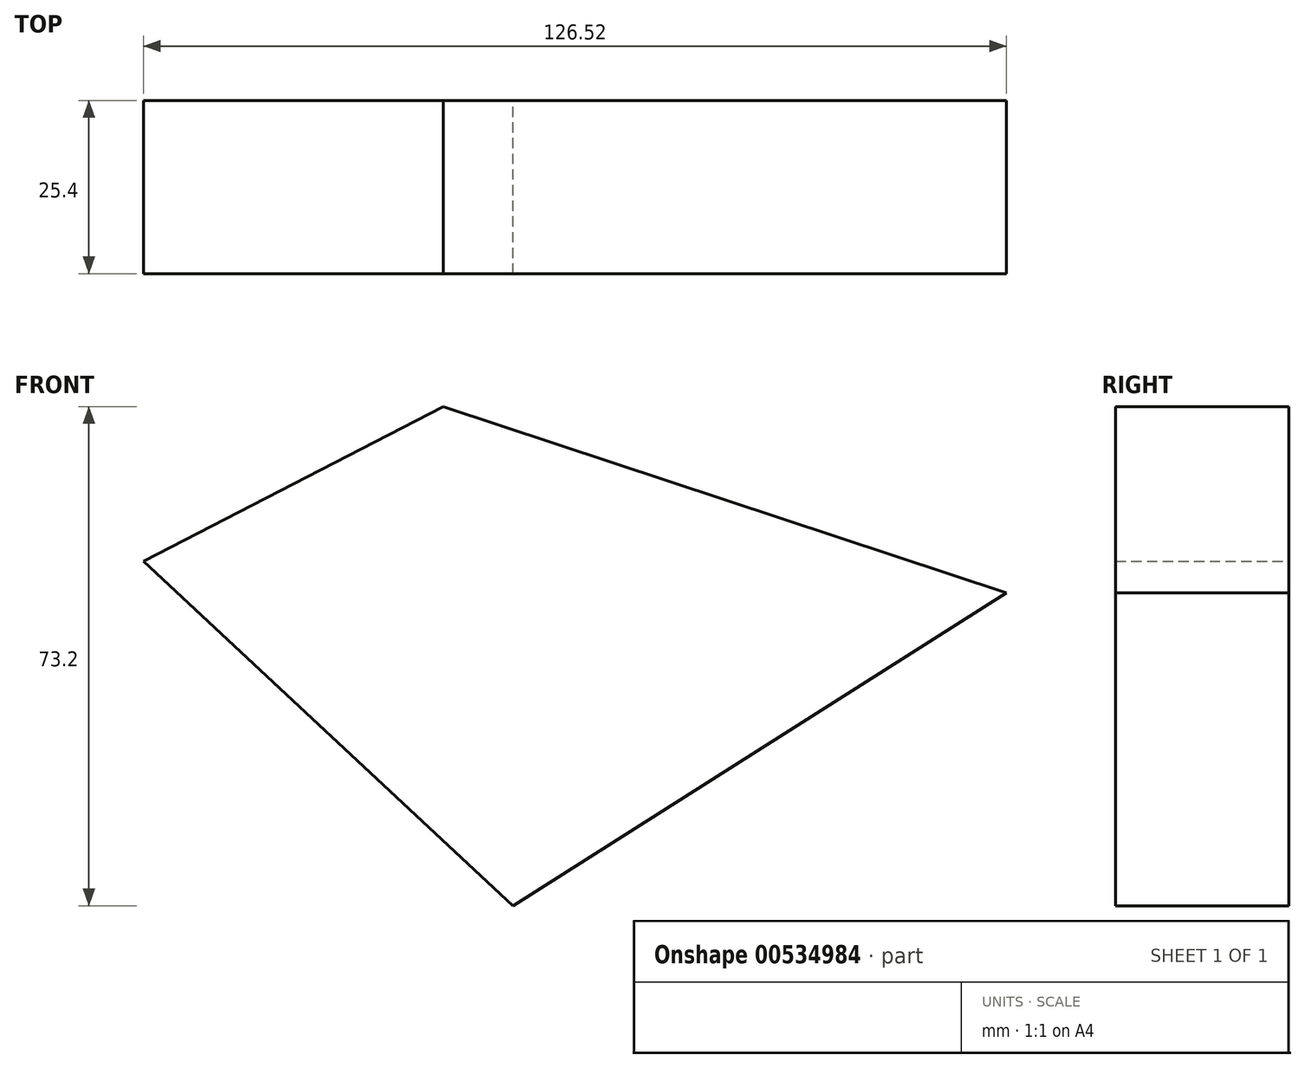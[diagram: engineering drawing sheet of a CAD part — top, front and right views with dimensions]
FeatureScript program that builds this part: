
annotation { "Feature Type Name" : "Feature", "Feature Type Description" : "" }
export const myFeature = defineFeature(function(context is Context, id is Id, definition is map)
    precondition{}
    {
        {
            var Q0;
            Q0=qCreatedBy(makeId("Front.planeOp"),FACE);
            var sketch = newSketch(context, id + "F0", { "sketchPlane" : qUnion([Q0])});
            skLineSegment(sketch, "E0", {"start": v(-32.49, 46.53) * mm, "end": v(-34.53, 44.67) * mm});
            skLineSegment(sketch, "E1", {"start": v(-34.53, 44.67) * mm, "end": v(-31.07, 40.86) * mm});
            skLineSegment(sketch, "E2", {"start": v(-31.07, 40.86) * mm, "end": v(-26.87, 44.67) * mm});
            skLineSegment(sketch, "E3", {"start": v(-26.87, 44.67) * mm, "end": v(-32.49, 46.53) * mm});
            skLineSegment(sketch, "E4", {"start": v(-31.07, 40.86) * mm, "end": v(-31.07, 26.95) * mm});
            skLineSegment(sketch, "E5", {"start": v(-31.07, 26.95) * mm, "end": v(-75.04, 4.26) * mm});
            skLineSegment(sketch, "E6", {"start": v(-75.04, 4.26) * mm, "end": v(-20.85, -46.25) * mm});
            skLineSegment(sketch, "E7", {"start": v(-20.85, -46.25) * mm, "end": v(52.06, 0) * mm});
            skLineSegment(sketch, "E8", {"start": v(52.06, -0.57) * mm, "end": v(-31.07, 26.95) * mm});
            skLineSegment(sketch, "E9", {"start": v(-20.85, -46.25) * mm, "end": v(-24.4, -50.05) * mm});
            skLineSegment(sketch, "E10", {"start": v(-20.85, -46.25) * mm, "end": v(-16.63, -50.19) * mm});
            skLineSegment(sketch, "E11", {"start": v(-24.4, -50.05) * mm, "end": v(-16.63, -50.19) * mm});
            skSolve(sketch);
        }
        {
            var Q0;
            {var subQ0=sQuery(id+"F0.wireOp",EDGE,"E5");Q0=makeQuery(id+"F0.imprint","IMPRINT",FACE,{"disambiguationData":[TD([[makeQuery(id+"F0.imprint","IMPRINT",EDGE,{"derivedFrom":subQ0}),1.0]])]});}
            extrude(context, id + "F1", {"entities" : qUnion([Q0]), "depth" : 25.4 * mm, "offsetDistance" : 25.4 * mm});
        }
    });
